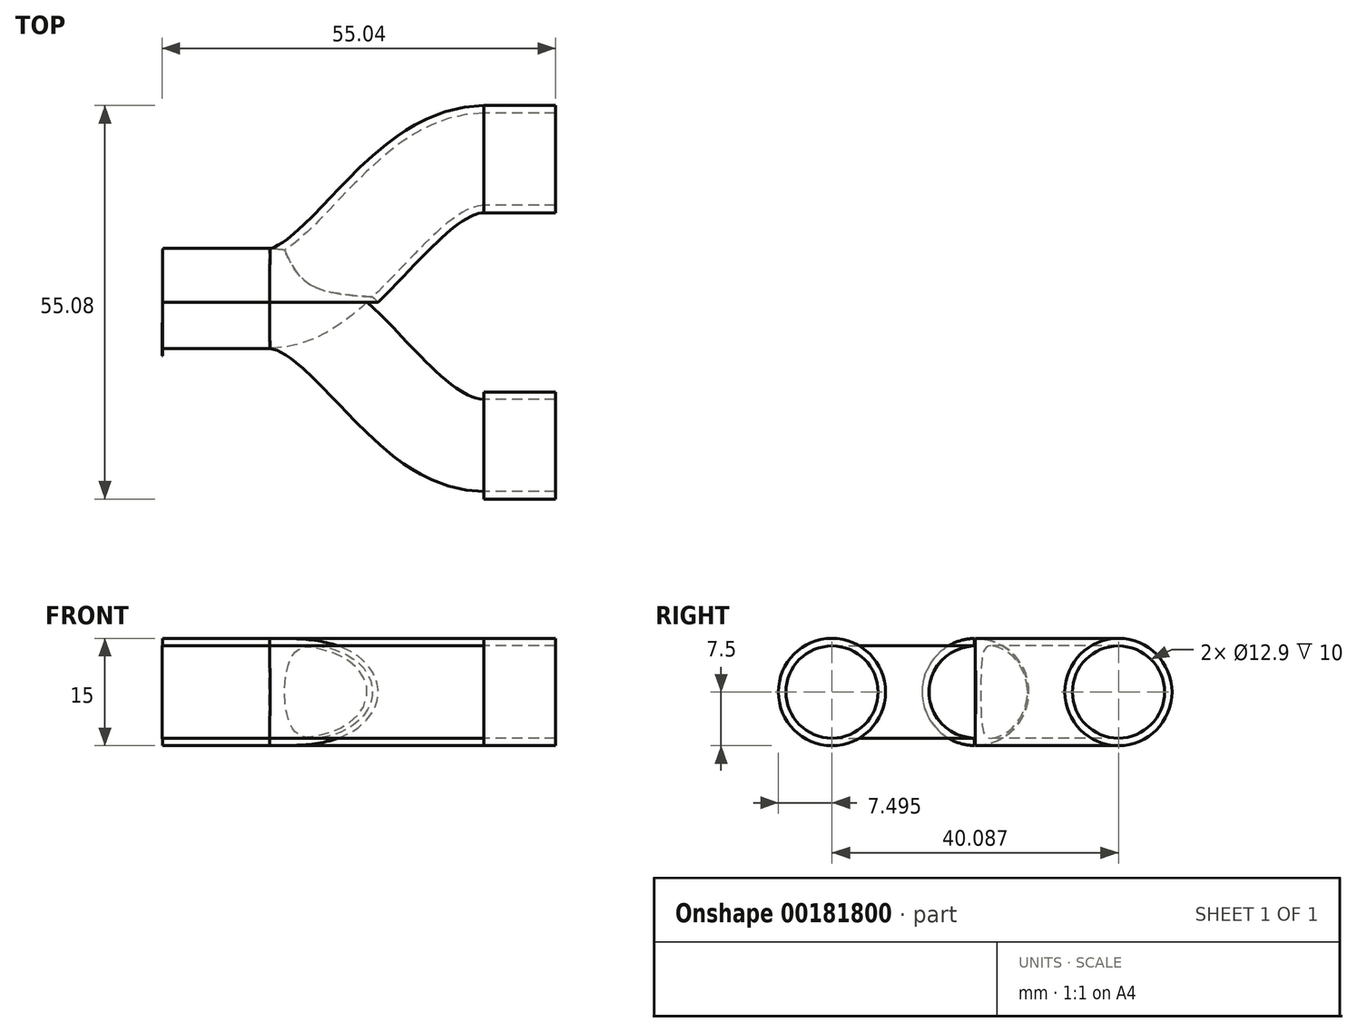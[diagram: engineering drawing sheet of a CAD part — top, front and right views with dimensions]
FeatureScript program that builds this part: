
annotation { "Feature Type Name" : "Feature", "Feature Type Description" : "" }
export const myFeature = defineFeature(function(context is Context, id is Id, definition is map)
    precondition{}
    {
        {
            var Q0;
            Q0=qCreatedBy(makeId("Top.planeOp"),FACE);
            var sketch = newSketch(context, id + "F0", { "sketchPlane" : qUnion([Q0])});
            skLineSegment(sketch, "E0", {"start": v(0, 20) * mm, "end": v(0, -20) * mm, "construction": true});
            skLineSegment(sketch, "E1", {"start": v(0, 0) * mm, "end": v(-30, 0) * mm, "construction": true});
            skFitSpline(sketch, "E2", {"points": [v(0, 20) * mm, v(-30, 0) * mm], "startDerivative": vector(-34.93, -0.21) * mm, "endDerivative": vector(-31.02, 0) * mm});
            skFitSpline(sketch, "E3.MirrorCS", {"points": [v(0, -20) * mm, v(-30, 0) * mm], "startDerivative": vector(-34.93, 0.21) * mm, "endDerivative": vector(-31.02, 0) * mm});
            skLineSegment(sketch, "E4", {"start": v(-30, 0) * mm, "end": v(-45, 0) * mm});
            skSolve(sketch);
        }
        {
            var Q0;
            Q0=qCreatedBy(makeId("Right.planeOp"),FACE);
            var sketch = newSketch(context, id + "F1", { "sketchPlane" : qUnion([Q0])});
            skCircle(sketch, "E5", {"center": v(20.15, 0) * mm, "radius": 7.5 * mm});
            skCircle(sketch, "E6", {"center": v(-19.93, 0) * mm, "radius": 7.5 * mm});
            skSolve(sketch);
        }
        {
            var Q0;
            Q0=makeQuery(id+"F1.imprint","IMPRINT",FACE,{"disambiguationData":[TD([[makeQuery(id+"F1.imprint","IMPRINT",EDGE,{"derivedFrom":sQuery(id+"F1.wireOp",EDGE,"E5")}),1.0]])]});
            var Q1;
            Q1=sQuery(id+"F0.wireOp",EDGE,"E2");
            var Q2;
            Q2=sQuery(id+"F0.wireOp",EDGE,"E4");
            sweep(context, id + "F2", {"profiles" : qUnion([Q0]), "path" : qUnion([Q1, Q2])});
        }
        {
            var Q0;
            Q0=makeQuery(id+"F1.imprint","IMPRINT",FACE,{"disambiguationData":[TD([[makeQuery(id+"F1.imprint","IMPRINT",EDGE,{"derivedFrom":sQuery(id+"F1.wireOp",EDGE,"E6")}),1.0]])]});
            var Q1;
            Q1=sQuery(id+"F0.wireOp",EDGE,"E3.MirrorCS");
            sweep(context, id + "F3", {"operationType" : NewBodyOperationType.ADD, "profiles" : qUnion([Q0]), "path" : qUnion([Q1])});
        }
        {
            var Q0;
            Q0=makeQuery(id+"F1.imprint","IMPRINT",FACE,{"disambiguationData":[TD([[makeQuery(id+"F1.imprint","IMPRINT",EDGE,{"derivedFrom":sQuery(id+"F1.wireOp",EDGE,"E6")}),1.0]])]});
            var sketch = newSketch(context, id + "F4", { "sketchPlane" : qUnion([Q0])});
            skCircle(sketch, "E7.0", {"center": v(-19.93, 0) * mm, "radius": 6.45 * mm});
            skCircle(sketch, "E8.0", {"center": v(20.15, 0) * mm, "radius": 6.45 * mm});
            skSolve(sketch);
        }
        {
            var Q0;
            Q0=makeQuery(id+"F4.imprint","IMPRINT",FACE,{"disambiguationData":[TD([[makeQuery(id+"F4.imprint","IMPRINT",EDGE,{"derivedFrom":sQuery(id+"F4.wireOp",EDGE,"E7.0")}),-1.0]])]});
            var Q1;
            Q1=sQuery(id+"F0.wireOp",EDGE,"E3.MirrorCS");
            var Q2;
            Q2=sQuery(id+"F0.wireOp",EDGE,"E4");
            sweep(context, id + "F5", {"operationType" : NewBodyOperationType.REMOVE, "profiles" : qUnion([Q0]), "path" : qUnion([Q1, Q2])});
        }
        {
            var Q0;
            Q0=makeQuery(id+"F4.imprint","IMPRINT",FACE,{"disambiguationData":[TD([[makeQuery(id+"F4.imprint","IMPRINT",EDGE,{"derivedFrom":sQuery(id+"F4.wireOp",EDGE,"E8.0")}),1.0]])]});
            var Q1;
            Q1=sQuery(id+"F0.wireOp",EDGE,"E2");
            var Q2;
            Q2=sQuery(id+"F0.wireOp",EDGE,"E4");
            sweep(context, id + "F6", {"operationType" : NewBodyOperationType.REMOVE, "profiles" : qUnion([Q0]), "path" : qUnion([Q1, Q2])});
        }
        {
            var Q0;
            Q0 = qSketchRegion(id + "F1", true);
            extrude(context, id + "F7", {"entities" : qUnion([Q0]), "operationType" : NewBodyOperationType.ADD, "depth" : 10 * mm});
        }
        {
            var Q0;
            Q0 = qSketchRegion(id + "F4", true);
            extrude(context, id + "F8", {"entities" : qUnion([Q0]), "operationType" : NewBodyOperationType.REMOVE, "depth" : 10 * mm});
        }
    });
